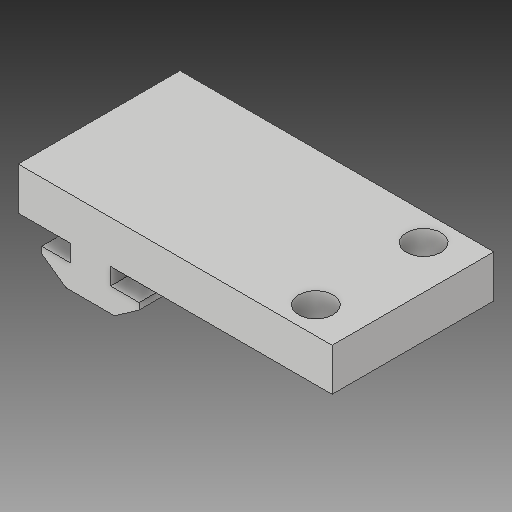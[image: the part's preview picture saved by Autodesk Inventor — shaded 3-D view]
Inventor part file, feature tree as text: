
AUTODESK INVENTOR PART (.ipt)
format: ipt  version: 2017 (Build 210142000, 142)  size: 130,048 bytes
history: native  units: in
note: dims shown in document units (in); Inventor stores cm internally (conversion verified against a paired STEP export)
features: sketch x2, extrude x1, hole x1
ambient origin geometry x8: Origin, YZ Plane, XZ Plane, XY Plane, X Axis, Y Axis, Z Axis, Center Point
bodies: Solid1 (feature_tree)
feature tree (4):
  extrude  "Extrusion1"  Depth=0.0787in
  hole  "Hole1"  [1 undecoded]
  sketch  "Sketch1"  dims[d0=0.6693in d2=0.1969in d3=0.0787in]
  sketch  "Sketch3"  dims[d4=0.1874in d6=0.4524in d7=0.1085in d8=0.225in d9=0.2221in d10=0.2409in d11=0.03in d12=0.03in d13=0.75in d14=0.0in d16=1.0268in d27=0.2in d28=0.2in d29=0.16in d30=0.75in d31=0.375in d32=0.25in d33=0.5635in d34=1.0in d35=0.8108in d36=0.125in d37=0.125in d50=0.9949in d51=0.1137in]
note: 1 required parameter value undecoded (feature->parameter linkage not recoverable at this tier; creation-order binding heuristic only, values carry confidence <= 0.55)
